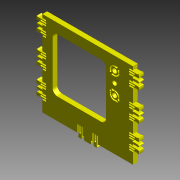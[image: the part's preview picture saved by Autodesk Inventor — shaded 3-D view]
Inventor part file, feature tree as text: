
AUTODESK INVENTOR PART (.ipt)
format: ipt  version: 2012 (Build 160160000, 160)  size: 658,944 bytes
history: native  units: in
note: dims shown in document units (in); Inventor stores cm internally (conversion verified against a paired STEP export)
features: other x4, extrude x2
ambient origin geometry x8: Origin, YZ Plane, XZ Plane, XY Plane, X Axis, Y Axis, Z Axis, Center Point
bodies: Solid1 (feature_tree)
feature tree (6):
  other  "skeleton.ipt"
  other  "POCKET_1-16"
  other  "STOCK_12MM"
  extrude  "Extrusion1"  Depth=0.3937in
  extrude  "Extrusion2"  Depth=0.4724in
  other  "THROUGH-CUT"
